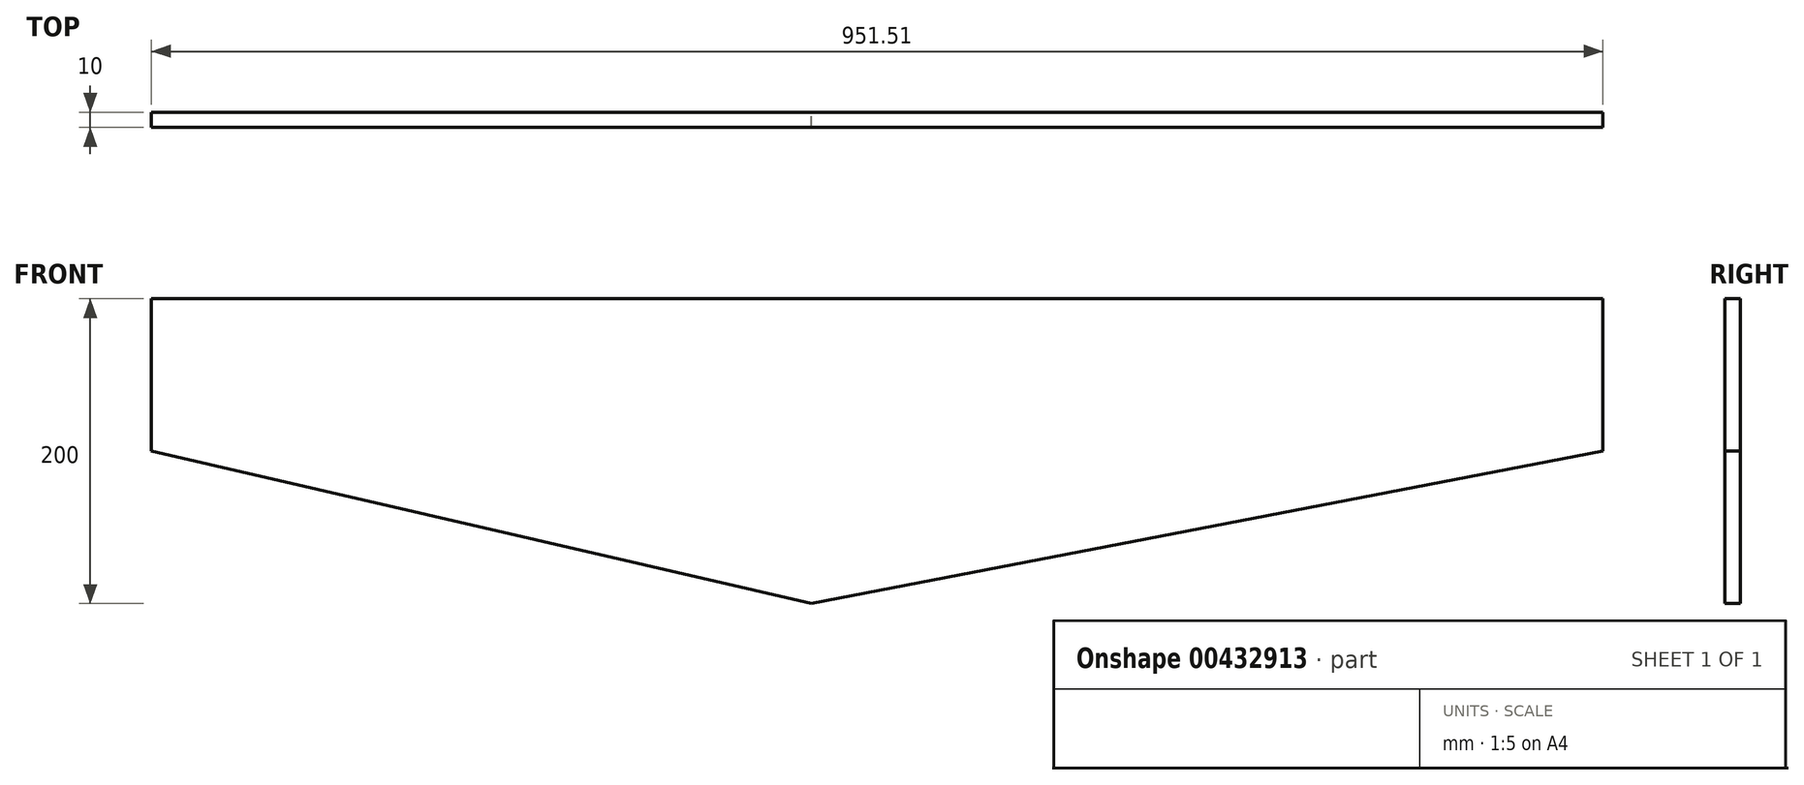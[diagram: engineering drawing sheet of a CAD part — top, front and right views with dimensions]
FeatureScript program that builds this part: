
annotation { "Feature Type Name" : "Feature", "Feature Type Description" : "" }
export const myFeature = defineFeature(function(context is Context, id is Id, definition is map)
    precondition{}
    {
        {
            var Q0;
            Q0=qCreatedBy(makeId("Front.planeOp"),FACE);
            var sketch = newSketch(context, id + "F0", { "sketchPlane" : qUnion([Q0])});
            skLineSegment(sketch, "E0", {"start": v(-432.7, 100) * mm, "end": v(518.82, 100) * mm});
            skLineSegment(sketch, "E1", {"start": v(518.82, 100) * mm, "end": v(518.82, 0) * mm});
            skLineSegment(sketch, "E2", {"start": v(518.82, 0) * mm, "end": v(0, -100) * mm});
            skLineSegment(sketch, "E3", {"start": v(0, -100) * mm, "end": v(-432.7, 0) * mm});
            skLineSegment(sketch, "E4", {"start": v(-432.7, 0) * mm, "end": v(-432.7, 100) * mm});
            skSolve(sketch);
        }
        {
            var Q0;
            Q0=makeQuery(id+"F0.imprint","IMPRINT",FACE,{"disambiguationData":[TD([[makeQuery(id+"F0.imprint","IMPRINT",EDGE,{"derivedFrom":sQuery(id+"F0.wireOp",EDGE,"E0")}),-1.0]])]});
            extrude(context, id + "F1", {"entities" : qUnion([Q0]), "depth" : 10 * mm});
        }
    });
